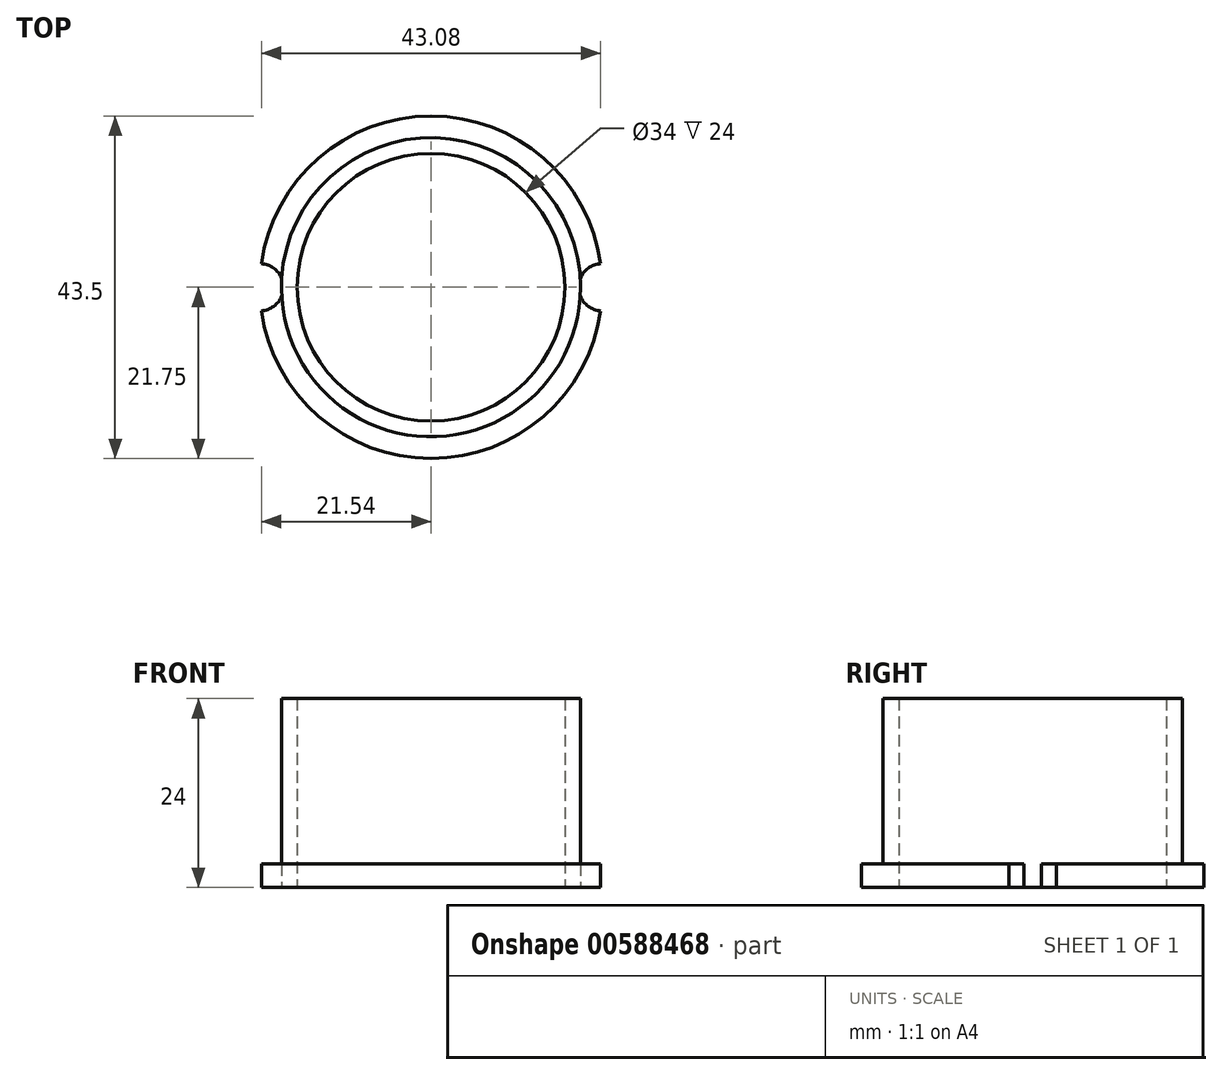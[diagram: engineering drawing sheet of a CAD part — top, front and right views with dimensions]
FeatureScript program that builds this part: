
annotation { "Feature Type Name" : "Feature", "Feature Type Description" : "" }
export const myFeature = defineFeature(function(context is Context, id is Id, definition is map)
    precondition{}
    {
        {
            var Q0;
            Q0=qCreatedBy(makeId("Top.planeOp"),FACE);
            var sketch = newSketch(context, id + "F0", { "sketchPlane" : qUnion([Q0])});
            skCircle(sketch, "E0", {"center": v(0, 0) * mm, "radius": 21.75 * mm});
            skCircle(sketch, "E1", {"center": v(21.75, 0) * mm, "radius": 3 * mm});
            skCircle(sketch, "E2", {"center": v(-21.75, 0) * mm, "radius": 3 * mm});
            skCircle(sketch, "E3", {"center": v(0, 0) * mm, "radius": 19 * mm});
            skCircle(sketch, "E4", {"center": v(0, 0) * mm, "radius": 17 * mm});
            skSolve(sketch);
        }
        {
            var Q0;
            {var subQ0=sQuery(id+"F0.wireOp",EDGE,"E2");var subQ1=sQuery(id+"F0.wireOp",EDGE,"E0");var subQ2=makeQuery(id+"F0.imprint","INTERSECT",VERTEX,{"disambiguationData":[OD(0.0)],"derivedFrom":[subQ1,subQ0]});Q0=makeQuery(id+"F0.imprint","IMPRINT",FACE,{"disambiguationData":[TD([[makeQuery(id+"F0.imprint","IMPRINT",EDGE,{"disambiguationData":[TD([[subQ2,1.0]])],"derivedFrom":subQ1}),1.0]])]});}
            var Q1;
            {var subQ0=sQuery(id+"F0.wireOp",EDGE,"E2");var subQ1=sQuery(id+"F0.wireOp",EDGE,"E0");var subQ2=makeQuery(id+"F0.imprint","INTERSECT",VERTEX,{"disambiguationData":[OD(1.0)],"derivedFrom":[subQ1,subQ0]});Q1=makeQuery(id+"F0.imprint","IMPRINT",FACE,{"disambiguationData":[TD([[makeQuery(id+"F0.imprint","IMPRINT",EDGE,{"disambiguationData":[TD([[subQ2,-1.0]])],"derivedFrom":subQ1}),1.0]])]});}
            var Q2;
            Q2=makeQuery(id+"F0.imprint","IMPRINT",FACE,{"disambiguationData":[TD([[makeQuery(id+"F0.imprint","IMPRINT",EDGE,{"derivedFrom":sQuery(id+"F0.wireOp",EDGE,"E4")}),-1.0]])]});
            extrude(context, id + "F1", {"entities" : qUnion([Q0, Q1, Q2]), "depth" : 3 * mm, "offsetDistance" : 25 * mm});
        }
        {
            var Q0;
            Q0=makeQuery(id+"F0.imprint","IMPRINT",FACE,{"disambiguationData":[TD([[makeQuery(id+"F0.imprint","IMPRINT",EDGE,{"derivedFrom":sQuery(id+"F0.wireOp",EDGE,"E3")}),1.0]])]});
            var Q1;
            {var subQ0=sQuery(id+"F0.wireOp",EDGE,"E3");var subQ1=sQuery(id+"F0.wireOp",EDGE,"E2");var subQ2=makeQuery(id+"F0.imprint","INTERSECT",VERTEX,{"disambiguationData":[OD(0.0)],"derivedFrom":[subQ1,subQ0]});Q1=makeQuery(id+"F0.imprint","IMPRINT",FACE,{"disambiguationData":[TD([[makeQuery(id+"F0.imprint","IMPRINT",EDGE,{"disambiguationData":[TD([[subQ2,1.0]])],"derivedFrom":subQ1}),1.0]])]});}
            var Q2;
            {var subQ0=sQuery(id+"F0.wireOp",EDGE,"E3");var subQ1=sQuery(id+"F0.wireOp",EDGE,"E1");var subQ2=makeQuery(id+"F0.imprint","INTERSECT",VERTEX,{"disambiguationData":[OD(0.0)],"derivedFrom":[subQ1,subQ0]});Q2=makeQuery(id+"F0.imprint","IMPRINT",FACE,{"disambiguationData":[TD([[makeQuery(id+"F0.imprint","IMPRINT",EDGE,{"disambiguationData":[TD([[subQ2,-1.0]])],"derivedFrom":subQ1}),1.0]])]});}
            extrude(context, id + "F2", {"entities" : qUnion([Q0, Q1, Q2]), "operationType" : NewBodyOperationType.ADD, "depth" : 24 * mm, "offsetDistance" : 25 * mm});
        }
    });
